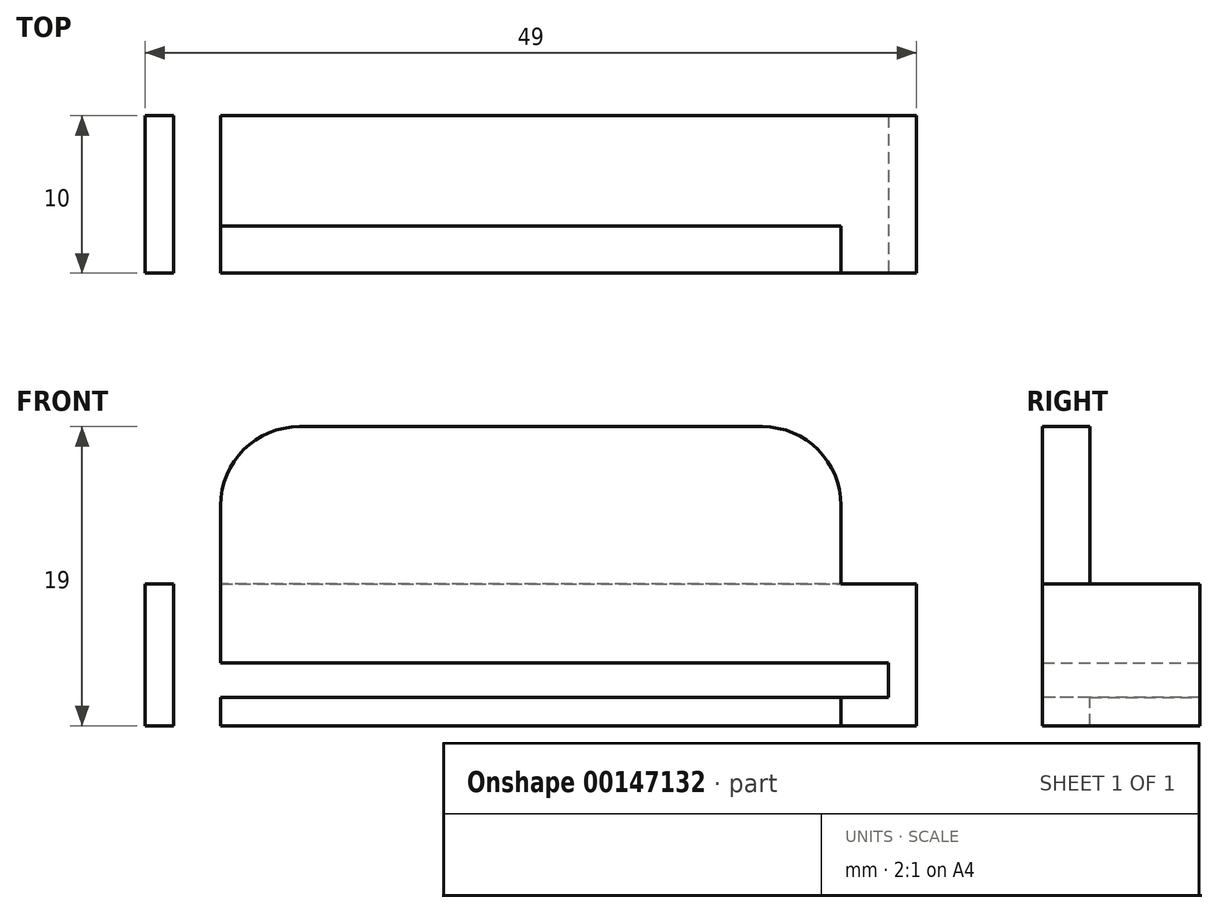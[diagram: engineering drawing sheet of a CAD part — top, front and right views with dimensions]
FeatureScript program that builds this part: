
annotation { "Feature Type Name" : "Feature", "Feature Type Description" : "" }
export const myFeature = defineFeature(function(context is Context, id is Id, definition is map)
    precondition{}
    {
        {
            var Q0;
            Q0=qCreatedBy(makeId("Top.planeOp"),FACE);
            var sketch = newSketch(context, id + "F0", { "sketchPlane" : qUnion([Q0])});
            skLineSegment(sketch, "E0.bottom", {"start": v(24.5, 5) * mm, "end": v(-24.5, 5) * mm});
            skLineSegment(sketch, "E0.top", {"start": v(24.5, -5) * mm, "end": v(-24.5, -5) * mm});
            skLineSegment(sketch, "E0.left", {"start": v(24.5, 5) * mm, "end": v(24.5, -5) * mm});
            skLineSegment(sketch, "E0.right", {"start": v(-24.5, 5) * mm, "end": v(-24.5, -5) * mm});
            skPoint(sketch, "E0.middle", {"position": v(0, 0) * mm});
            skLineSegment(sketch, "E1.0", {"start": v(22.5, -2) * mm, "end": v(-22.5, -2) * mm});
            skLineSegment(sketch, "E2", {"start": v(-24.5, 5) * mm, "end": v(-22.7, 5) * mm});
            skLineSegment(sketch, "E3", {"start": v(-22.7, 5) * mm, "end": v(-22.7, -5) * mm});
            skLineSegment(sketch, "E4", {"start": v(-22.7, -5) * mm, "end": v(-19.7, -5) * mm});
            skLineSegment(sketch, "E5", {"start": v(-19.7, -5) * mm, "end": v(-19.7, 5) * mm});
            skLineSegment(sketch, "E6", {"start": v(24.5, 5) * mm, "end": v(22.7, 5) * mm});
            skLineSegment(sketch, "E7", {"start": v(22.7, 5) * mm, "end": v(19.7, 5) * mm});
            skLineSegment(sketch, "E8", {"start": v(19.7, 5) * mm, "end": v(19.7, -5) * mm});
            skLineSegment(sketch, "E9", {"start": v(22.7, 5) * mm, "end": v(22.7, -5) * mm});
            skSolve(sketch);
        }
        {
            var Q0;
            {var subQ0=sQuery(id+"F0.wireOp",EDGE,"E2");Q0=makeQuery(id+"F0.imprint","IMPRINT",FACE,{"disambiguationData":[TD([[makeQuery(id+"F0.imprint","IMPRINT",EDGE,{"derivedFrom":subQ0}),-1.0]])]});}
            var Q1;
            {var subQ3=sQuery(id+"F0.wireOp",EDGE,"E5");var subQ5=sQuery(id+"F0.wireOp",EDGE,"E1.0");var subQ7=makeQuery(id+"F0.imprint","INTERSECT",VERTEX,{"derivedFrom":[subQ5,subQ3]});Q1=makeQuery(id+"F0.imprint","IMPRINT",FACE,{"disambiguationData":[TD([[makeQuery(id+"F0.imprint","IMPRINT",EDGE,{"disambiguationData":[TD([[subQ7,-1.0]])],"derivedFrom":subQ5}),-1.0]])]});}
            var Q2;
            {var subQ0=sQuery(id+"F0.wireOp",EDGE,"E8");var subQ5=sQuery(id+"F0.wireOp",EDGE,"E1.0");var subQ6=makeQuery(id+"F0.imprint","INTERSECT",VERTEX,{"derivedFrom":[subQ5,subQ0]});Q2=makeQuery(id+"F0.imprint","IMPRINT",FACE,{"disambiguationData":[TD([[makeQuery(id+"F0.imprint","IMPRINT",EDGE,{"disambiguationData":[TD([[subQ6,-1.0]])],"derivedFrom":subQ5}),-1.0]])]});}
            var Q3;
            {var subQ5=sQuery(id+"F0.wireOp",EDGE,"E7");Q3=makeQuery(id+"F0.imprint","IMPRINT",FACE,{"disambiguationData":[TD([[makeQuery(id+"F0.imprint","IMPRINT",EDGE,{"derivedFrom":subQ5}),1.0]])]});}
            var Q4;
            {var subQ0=sQuery(id+"F0.wireOp",EDGE,"E6");Q4=makeQuery(id+"F0.imprint","IMPRINT",FACE,{"disambiguationData":[TD([[makeQuery(id+"F0.imprint","IMPRINT",EDGE,{"derivedFrom":subQ0}),1.0]])]});}
            var Q5;
            {var subQ0=sQuery(id+"F0.wireOp",EDGE,"E0.left");var subQ1=sQuery(id+"F0.wireOp",EDGE,"E0.top");var subQ2=makeQuery(id+"F0.imprint","INTERSECT",VERTEX,{"derivedFrom":[subQ1,subQ0]});Q5=makeQuery(id+"F0.imprint","IMPRINT",FACE,{"disambiguationData":[TD([[makeQuery(id+"F0.imprint","IMPRINT",EDGE,{"disambiguationData":[TD([[subQ2,-1.0]])],"derivedFrom":subQ1}),-1.0]])]});}
            var Q6;
            {var subQ0=sQuery(id+"F0.wireOp",EDGE,"E8");var subQ1=sQuery(id+"F0.wireOp",EDGE,"E0.top");var subQ2=makeQuery(id+"F0.imprint","INTERSECT",VERTEX,{"derivedFrom":[subQ1,subQ0]});Q6=makeQuery(id+"F0.imprint","IMPRINT",FACE,{"disambiguationData":[TD([[makeQuery(id+"F0.imprint","IMPRINT",EDGE,{"disambiguationData":[TD([[subQ2,1.0]])],"derivedFrom":subQ1}),-1.0]])]});}
            var Q7;
            {var subQ3=sQuery(id+"F0.wireOp",EDGE,"E8");var subQ5=sQuery(id+"F0.wireOp",EDGE,"E1.0");var subQ7=makeQuery(id+"F0.imprint","INTERSECT",VERTEX,{"derivedFrom":[subQ5,subQ3]});Q7=makeQuery(id+"F0.imprint","IMPRINT",FACE,{"disambiguationData":[TD([[makeQuery(id+"F0.imprint","IMPRINT",EDGE,{"disambiguationData":[TD([[subQ7,-1.0]])],"derivedFrom":subQ5}),1.0]])]});}
            var Q8;
            {var subQ5=sQuery(id+"F0.wireOp",EDGE,"E4");Q8=makeQuery(id+"F0.imprint","IMPRINT",FACE,{"disambiguationData":[TD([[makeQuery(id+"F0.imprint","IMPRINT",EDGE,{"derivedFrom":subQ5}),1.0]])]});}
            var Q9;
            {var subQ0=sQuery(id+"F0.wireOp",EDGE,"E0.right");var subQ1=sQuery(id+"F0.wireOp",EDGE,"E0.top");var subQ2=makeQuery(id+"F0.imprint","INTERSECT",VERTEX,{"derivedFrom":[subQ1,subQ0]});Q9=makeQuery(id+"F0.imprint","IMPRINT",FACE,{"disambiguationData":[TD([[makeQuery(id+"F0.imprint","IMPRINT",EDGE,{"disambiguationData":[TD([[subQ2,1.0]])],"derivedFrom":subQ0}),1.0]])]});}
            extrude(context, id + "F1", {"entities" : qUnion([Q0, Q1, Q2, Q3, Q4, Q5, Q6, Q7, Q8, Q9]), "depth" : 5 * mm});
        }
        {
            var Q0;
            {var subQ0=sQuery(id+"F0.wireOp",EDGE,"E0.right");var subQ1=sQuery(id+"F0.wireOp",EDGE,"E0.top");var subQ2=makeQuery(id+"F0.imprint","INTERSECT",VERTEX,{"derivedFrom":[subQ1,subQ0]});Q0=makeQuery(id+"F0.imprint","IMPRINT",FACE,{"disambiguationData":[TD([[makeQuery(id+"F0.imprint","IMPRINT",EDGE,{"disambiguationData":[TD([[subQ2,1.0]])],"derivedFrom":subQ0}),1.0]])]});}
            var Q1;
            {var subQ0=sQuery(id+"F0.wireOp",EDGE,"E2");Q1=makeQuery(id+"F0.imprint","IMPRINT",FACE,{"disambiguationData":[TD([[makeQuery(id+"F0.imprint","IMPRINT",EDGE,{"derivedFrom":subQ0}),-1.0]])]});}
            var Q2;
            {var subQ0=sQuery(id+"F0.wireOp",EDGE,"E0.left");var subQ1=sQuery(id+"F0.wireOp",EDGE,"E0.top");var subQ2=makeQuery(id+"F0.imprint","INTERSECT",VERTEX,{"derivedFrom":[subQ1,subQ0]});Q2=makeQuery(id+"F0.imprint","IMPRINT",FACE,{"disambiguationData":[TD([[makeQuery(id+"F0.imprint","IMPRINT",EDGE,{"disambiguationData":[TD([[subQ2,-1.0]])],"derivedFrom":subQ1}),-1.0]])]});}
            var Q3;
            {var subQ0=sQuery(id+"F0.wireOp",EDGE,"E6");Q3=makeQuery(id+"F0.imprint","IMPRINT",FACE,{"disambiguationData":[TD([[makeQuery(id+"F0.imprint","IMPRINT",EDGE,{"derivedFrom":subQ0}),1.0]])]});}
            extrude(context, id + "F2", {"entities" : qUnion([Q0, Q1, Q2, Q3]), "operationType" : NewBodyOperationType.ADD, "oppositeDirection" : true, "depth" : 2 * mm});
        }
        {
            var Q0;
            {var subQ5=sQuery(id+"F0.wireOp",EDGE,"E4");Q0=makeQuery(id+"F0.imprint","IMPRINT",FACE,{"disambiguationData":[TD([[makeQuery(id+"F0.imprint","IMPRINT",EDGE,{"derivedFrom":subQ5}),1.0]])]});}
            var Q1;
            {var subQ3=sQuery(id+"F0.wireOp",EDGE,"E5");var subQ5=sQuery(id+"F0.wireOp",EDGE,"E1.0");var subQ7=makeQuery(id+"F0.imprint","INTERSECT",VERTEX,{"derivedFrom":[subQ5,subQ3]});Q1=makeQuery(id+"F0.imprint","IMPRINT",FACE,{"disambiguationData":[TD([[makeQuery(id+"F0.imprint","IMPRINT",EDGE,{"disambiguationData":[TD([[subQ7,-1.0]])],"derivedFrom":subQ5}),-1.0]])]});}
            var Q2;
            {var subQ0=sQuery(id+"F0.wireOp",EDGE,"E8");var subQ1=sQuery(id+"F0.wireOp",EDGE,"E0.top");var subQ2=makeQuery(id+"F0.imprint","INTERSECT",VERTEX,{"derivedFrom":[subQ1,subQ0]});Q2=makeQuery(id+"F0.imprint","IMPRINT",FACE,{"disambiguationData":[TD([[makeQuery(id+"F0.imprint","IMPRINT",EDGE,{"disambiguationData":[TD([[subQ2,1.0]])],"derivedFrom":subQ1}),-1.0]])]});}
            var Q3;
            {var subQ5=sQuery(id+"F0.wireOp",EDGE,"E7");Q3=makeQuery(id+"F0.imprint","IMPRINT",FACE,{"disambiguationData":[TD([[makeQuery(id+"F0.imprint","IMPRINT",EDGE,{"derivedFrom":subQ5}),1.0]])]});}
            extrude(context, id + "F3", {"entities" : qUnion([Q0, Q1, Q2, Q3]), "operationType" : NewBodyOperationType.ADD, "oppositeDirection" : true, "depth" : 4 * mm, "hasSecondDirection" : true, "secondDirectionOppositeDirection" : true, "secondDirectionDepth" : 2.2 * mm});
        }
        {
            var Q0;
            {var subQ0=sQuery(id+"F0.wireOp",EDGE,"E0.right");var subQ1=sQuery(id+"F0.wireOp",EDGE,"E0.top");var subQ2=makeQuery(id+"F0.imprint","INTERSECT",VERTEX,{"derivedFrom":[subQ1,subQ0]});Q0=makeQuery(id+"F0.imprint","IMPRINT",FACE,{"disambiguationData":[TD([[makeQuery(id+"F0.imprint","IMPRINT",EDGE,{"disambiguationData":[TD([[subQ2,1.0]])],"derivedFrom":subQ0}),1.0]])]});}
            var Q1;
            {var subQ0=sQuery(id+"F0.wireOp",EDGE,"E2");Q1=makeQuery(id+"F0.imprint","IMPRINT",FACE,{"disambiguationData":[TD([[makeQuery(id+"F0.imprint","IMPRINT",EDGE,{"derivedFrom":subQ0}),-1.0]])]});}
            var Q2;
            {var subQ0=sQuery(id+"F0.wireOp",EDGE,"E0.left");var subQ1=sQuery(id+"F0.wireOp",EDGE,"E0.top");var subQ2=makeQuery(id+"F0.imprint","INTERSECT",VERTEX,{"derivedFrom":[subQ1,subQ0]});Q2=makeQuery(id+"F0.imprint","IMPRINT",FACE,{"disambiguationData":[TD([[makeQuery(id+"F0.imprint","IMPRINT",EDGE,{"disambiguationData":[TD([[subQ2,-1.0]])],"derivedFrom":subQ1}),-1.0]])]});}
            var Q3;
            {var subQ0=sQuery(id+"F0.wireOp",EDGE,"E6");Q3=makeQuery(id+"F0.imprint","IMPRINT",FACE,{"disambiguationData":[TD([[makeQuery(id+"F0.imprint","IMPRINT",EDGE,{"derivedFrom":subQ0}),1.0]])]});}
            extrude(context, id + "F4", {"entities" : qUnion([Q0, Q1, Q2, Q3]), "operationType" : NewBodyOperationType.ADD, "oppositeDirection" : true, "depth" : 4 * mm, "hasSecondDirection" : true, "secondDirectionOppositeDirection" : true, "secondDirectionDepth" : 2 * mm});
        }
        {
            var Q0;
            {var subQ0=sQuery(id+"F0.wireOp",EDGE,"E5");var subQ5=sQuery(id+"F0.wireOp",EDGE,"E1.0");var subQ6=makeQuery(id+"F0.imprint","INTERSECT",VERTEX,{"derivedFrom":[subQ5,subQ0]});Q0=makeQuery(id+"F0.imprint","IMPRINT",FACE,{"disambiguationData":[TD([[makeQuery(id+"F0.imprint","IMPRINT",EDGE,{"disambiguationData":[TD([[subQ6,1.0]])],"derivedFrom":subQ5}),1.0]])]});}
            extrude(context, id + "F5", {"entities" : qUnion([Q0]), "operationType" : NewBodyOperationType.ADD, "depth" : 15 * mm});
        }
        {
            var Q0;
            Q0=makeQuery(id+"F5.opExtrude","CAP_EDGE",EDGE,{"disambiguationData":[OSD([sQuery(id+"F0.wireOp",EDGE,"E5")])],"isStart":false});
            var Q1;
            Q1=makeQuery(id+"F5.opExtrude","CAP_EDGE",EDGE,{"disambiguationData":[OSD([sQuery(id+"F0.wireOp",EDGE,"E8")])],"isStart":false});
            fillet(context, id + "F6", {"entities" : qUnion([Q0, Q1]), "radius" : 5 * mm, "tangentPropagation" : true, "allowEdgeOverflow" : false});
        }
    });
